# Revit family: OPUS-XBOX2
name_source: partatom
category: Mechanical Equipment
revit_build: Autodesk Revit 2015 (Build: 20140606_1530(x64)
units: mm (PartAtom-declared; Revit-internal decimal feet)

## types (1)
- OPUS-XBOX2
    Apparent Load = 161 VA
    Catalogue Pages = http://www.nuaire.co.uk
    Classification.Uniclass.Pr.Description = Centrifugal fans
    Classification.Uniclass.Pr.Number = Pr_65_67_29_12
    Description = Heat Recovery Unit
    Electrical Phase = 1
    Fax Number = +44(0)2920-858-222
    Full Load Current = 1 A
    Height = 185 mm
    I&M Manual = http://www.nuaire.co.uk
    IFCExportAs = IfcAirToAirHeatRecoveryType
    Length = 850 mm  [stored 2.78871 ft]
    Manufacturer = Nuaire
    Manufacturer Name = Nuaire
    Maximum Ambient Temperature = 40 °C
    Model = OPUS-XBOX
    Nominal Motor Rating = 0 kW
    Nuaire Model Code = OPUS-XBOX
    Number of Connection Poles = 2
    OmniClass Number = 23-33 31 19 13
    OmniClass Title = Centrifugal fans
    Postcode = CF83 1NA
    Revit Family Last Revised = IfcAirToAirHeatRecoveryType
    Starting Current = 1 A
    Telephone Number = +44(0)2920-858-200
    URL = http://www.nuaire.co.uk
    Unit Description = Heat Recovery Unit
    VAT Registration Number = 877308
    Voltage = 230 V
    Warranty Period = 5 Years
    Weatherproof or Internal Only = Internal
    Weight = 25.00 kg
    Width = 685 mm

note: [stored X ft] marks values corroborated as IEEE doubles in the binary element streams (Revit-internal decimal feet)

## geometry (parser evidence)
native form markers: Blend x8, Sweep x7
no freeform markers — native parametric forms only
